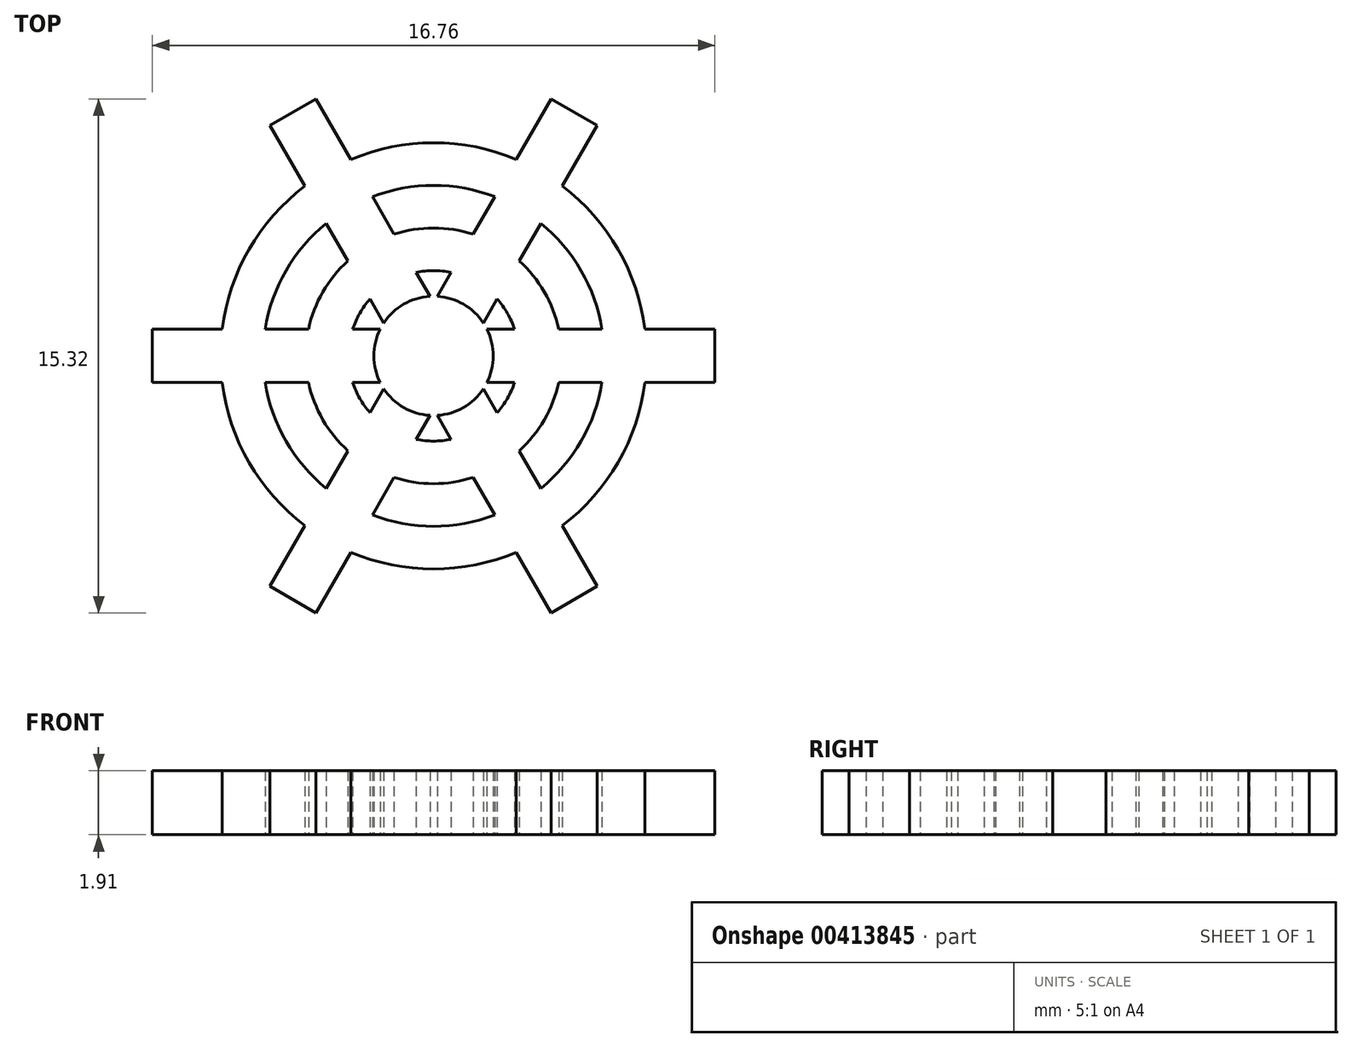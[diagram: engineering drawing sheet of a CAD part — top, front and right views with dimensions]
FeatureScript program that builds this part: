
annotation { "Feature Type Name" : "Feature", "Feature Type Description" : "" }
export const myFeature = defineFeature(function(context is Context, id is Id, definition is map)
    precondition{}
    {
        {
            var Q0;
            Q0=qCreatedBy(makeId("Top.planeOp"),FACE);
            var sketch = newSketch(context, id + "F0", { "sketchPlane" : qUnion([Q0])});
            skArc(sketch, "E0", {"start": v(-3.84, 5.06) * mm, "mid": v(-5.5, 3.17) * mm, "end": v(-6.3, 0.8) * mm});
            skArc(sketch, "E1", {"start": v(-3.2, 3.95) * mm, "mid": v(-4.4, 2.54) * mm, "end": v(-5.02, 0.8) * mm});
            skArc(sketch, "E2", {"start": v(-2.55, 2.83) * mm, "mid": v(-3.3, 1.9) * mm, "end": v(-3.73, 0.8) * mm});
            skArc(sketch, "E3", {"start": v(-1.9, 1.7) * mm, "mid": v(-2.2, 1.27) * mm, "end": v(-2.41, 0.8) * mm});
            skLineSegment(sketch, "E4.bottom", {"start": v(8.38, -0.8) * mm, "end": v(6.3, -0.8) * mm});
            skLineSegment(sketch, "E4.top", {"start": v(8.38, 0.8) * mm, "end": v(6.3, 0.8) * mm});
            skLineSegment(sketch, "E4.left", {"start": v(8.38, -0.8) * mm, "end": v(8.38, 0.8) * mm});
            skLineSegment(sketch, "E4.right", {"start": v(-8.38, -0.8) * mm, "end": v(-8.38, 0.8) * mm});
            skLineSegment(sketch, "E5.top", {"start": v(0.8, -8.38) * mm, "end": v(-0.8, -8.38) * mm});
            skLineSegment(sketch, "E6.1.1", {"start": v(-3.5, 7.66) * mm, "end": v(-2.46, 5.85) * mm});
            skLineSegment(sketch, "E6.1.2", {"start": v(-3.5, 7.66) * mm, "end": v(-4.88, 6.86) * mm});
            skLineSegment(sketch, "E6.1.3", {"start": v(-4.88, 6.86) * mm, "end": v(-3.84, 5.06) * mm});
            skLineSegment(sketch, "E6.1.4", {"start": v(4.88, -6.86) * mm, "end": v(3.5, -7.66) * mm});
            skLineSegment(sketch, "E6.2.1", {"start": v(-4.88, -6.86) * mm, "end": v(-3.84, -5.06) * mm});
            skLineSegment(sketch, "E6.2.2", {"start": v(-4.88, -6.86) * mm, "end": v(-3.5, -7.66) * mm});
            skLineSegment(sketch, "E6.2.3", {"start": v(-3.5, -7.66) * mm, "end": v(-2.46, -5.85) * mm});
            skLineSegment(sketch, "E6.2.4", {"start": v(3.5, 7.66) * mm, "end": v(4.88, 6.86) * mm});
            skLineSegment(sketch, "E7.trimOffspring", {"start": v(-3.2, 3.95) * mm, "end": v(-2.55, 2.83) * mm});
            skLineSegment(sketch, "E8.trimOffspring", {"start": v(-1.82, 4.74) * mm, "end": v(-1.18, 3.62) * mm});
            skLineSegment(sketch, "E9.trimOffspring", {"start": v(-1.9, 1.7) * mm, "end": v(-1.48, 0.98) * mm});
            skLineSegment(sketch, "E10.trimOffspring", {"start": v(-0.52, 2.49) * mm, "end": v(-0.1, 1.77) * mm});
            skArc(sketch, "E11.trimOffspring", {"start": v(-6.3, -0.8) * mm, "mid": v(-5.5, -3.17) * mm, "end": v(-3.84, -5.06) * mm});
            skArc(sketch, "E12.trimOffspring", {"start": v(-5.02, -0.8) * mm, "mid": v(-4.4, -2.54) * mm, "end": v(-3.2, -3.95) * mm});
            skLineSegment(sketch, "E13.trimOffspring", {"start": v(-6.3, 0.8) * mm, "end": v(-8.38, 0.8) * mm});
            skLineSegment(sketch, "E14.trimOffspring", {"start": v(-6.3, -0.8) * mm, "end": v(-8.38, -0.8) * mm});
            skArc(sketch, "E15.trimOffspring", {"start": v(-3.73, -0.8) * mm, "mid": v(-3.3, -1.9) * mm, "end": v(-2.55, -2.83) * mm});
            skLineSegment(sketch, "E16.trimOffspring", {"start": v(-3.73, 0.8) * mm, "end": v(-5.02, 0.8) * mm});
            skLineSegment(sketch, "E17.trimOffspring", {"start": v(-3.73, -0.8) * mm, "end": v(-5.02, -0.8) * mm});
            skArc(sketch, "E18.trimOffspring", {"start": v(-2.41, -0.8) * mm, "mid": v(-2.2, -1.27) * mm, "end": v(-1.9, -1.7) * mm});
            skLineSegment(sketch, "E19.trimOffspring", {"start": v(0.1, -1.77) * mm, "end": v(0.52, -2.49) * mm});
            skLineSegment(sketch, "E20.trimOffspring", {"start": v(-1.6, 0.8) * mm, "end": v(-2.41, 0.8) * mm});
            skLineSegment(sketch, "E21.trimOffspring", {"start": v(0.1, 1.77) * mm, "end": v(0.52, 2.49) * mm});
            skLineSegment(sketch, "E22.trimOffspring", {"start": v(-3.2, -3.95) * mm, "end": v(-2.55, -2.83) * mm});
            skArc(sketch, "E23.trimOffspring", {"start": v(-2.46, -5.85) * mm, "mid": v(0, -6.35) * mm, "end": v(2.46, -5.85) * mm});
            skLineSegment(sketch, "E24.trimOffspring", {"start": v(-1.82, -4.74) * mm, "end": v(-1.18, -3.62) * mm});
            skLineSegment(sketch, "E25.trimOffspring", {"start": v(2.46, -5.85) * mm, "end": v(3.5, -7.66) * mm});
            skArc(sketch, "E26.trimOffspring", {"start": v(3.84, -5.06) * mm, "mid": v(5.5, -3.17) * mm, "end": v(6.3, -0.8) * mm});
            skLineSegment(sketch, "E27.trimOffspring", {"start": v(3.84, -5.06) * mm, "end": v(4.88, -6.86) * mm});
            skLineSegment(sketch, "E28.trimOffspring", {"start": v(5.02, -0.8) * mm, "end": v(3.73, -0.8) * mm});
            skArc(sketch, "E29.trimOffspring", {"start": v(6.3, 0.8) * mm, "mid": v(5.5, 3.17) * mm, "end": v(3.84, 5.06) * mm});
            skLineSegment(sketch, "E30.trimOffspring", {"start": v(5.02, 0.8) * mm, "end": v(3.73, 0.8) * mm});
            skLineSegment(sketch, "E31.trimOffspring", {"start": v(3.84, 5.06) * mm, "end": v(4.88, 6.86) * mm});
            skArc(sketch, "E32.trimOffspring", {"start": v(2.46, 5.85) * mm, "mid": v(0, 6.35) * mm, "end": v(-2.46, 5.85) * mm});
            skLineSegment(sketch, "E33.trimOffspring", {"start": v(2.46, 5.85) * mm, "end": v(3.5, 7.66) * mm});
            skArc(sketch, "E34.trimOffspring", {"start": v(1.82, 4.74) * mm, "mid": v(0, 5.08) * mm, "end": v(-1.82, 4.74) * mm});
            skArc(sketch, "E35.trimOffspring", {"start": v(1.18, 3.62) * mm, "mid": v(0, 3.81) * mm, "end": v(-1.18, 3.62) * mm});
            skArc(sketch, "E36.trimOffspring", {"start": v(0.52, 2.49) * mm, "mid": v(0, 2.54) * mm, "end": v(-0.52, 2.49) * mm});
            skLineSegment(sketch, "E37.trimOffspring", {"start": v(1.18, 3.62) * mm, "end": v(1.82, 4.74) * mm});
            skLineSegment(sketch, "E38.trimOffspring", {"start": v(2.55, 2.83) * mm, "end": v(3.2, 3.95) * mm});
            skLineSegment(sketch, "E39.trimOffspring", {"start": v(2.41, 0.8) * mm, "end": v(1.6, 0.8) * mm});
            skLineSegment(sketch, "E40.trimOffspring", {"start": v(2.41, -0.8) * mm, "end": v(1.6, -0.8) * mm});
            skLineSegment(sketch, "E41.trimOffspring", {"start": v(2.55, -2.83) * mm, "end": v(3.2, -3.95) * mm});
            skLineSegment(sketch, "E42.trimOffspring", {"start": v(1.18, -3.62) * mm, "end": v(1.82, -4.74) * mm});
            skLineSegment(sketch, "E43.trimOffspring", {"start": v(-0.52, -2.49) * mm, "end": v(-0.1, -1.77) * mm});
            skLineSegment(sketch, "E44.trimOffspring", {"start": v(-1.9, -1.7) * mm, "end": v(-1.48, -0.98) * mm});
            skArc(sketch, "E45.trimOffspring", {"start": v(-1.18, -3.62) * mm, "mid": v(0, -3.81) * mm, "end": v(1.18, -3.62) * mm});
            skArc(sketch, "E46.trimOffspring", {"start": v(-1.82, -4.74) * mm, "mid": v(0, -5.08) * mm, "end": v(1.82, -4.74) * mm});
            skArc(sketch, "E47.trimOffspring", {"start": v(2.55, -2.83) * mm, "mid": v(3.3, -1.9) * mm, "end": v(3.73, -0.8) * mm});
            skArc(sketch, "E48.trimOffspring", {"start": v(3.2, -3.95) * mm, "mid": v(4.4, -2.54) * mm, "end": v(5.02, -0.8) * mm});
            skArc(sketch, "E49.trimOffspring", {"start": v(5.02, 0.8) * mm, "mid": v(4.4, 2.54) * mm, "end": v(3.2, 3.95) * mm});
            skArc(sketch, "E50.trimOffspring", {"start": v(3.73, 0.8) * mm, "mid": v(3.3, 1.9) * mm, "end": v(2.55, 2.83) * mm});
            skArc(sketch, "E51.trimOffspring", {"start": v(2.41, 0.8) * mm, "mid": v(2.2, 1.27) * mm, "end": v(1.9, 1.7) * mm});
            skLineSegment(sketch, "E52.trimOffspring", {"start": v(1.48, 0.98) * mm, "end": v(1.9, 1.7) * mm});
            skLineSegment(sketch, "E53.trimOffspring", {"start": v(1.48, -0.98) * mm, "end": v(1.9, -1.7) * mm});
            skLineSegment(sketch, "E54.trimOffspring", {"start": v(-1.6, -0.8) * mm, "end": v(-2.41, -0.8) * mm});
            skArc(sketch, "E55", {"start": v(-1.6, 0.8) * mm, "mid": v(-1.78, 0) * mm, "end": v(-1.6, -0.8) * mm});
            skArc(sketch, "E56.trimOffspring", {"start": v(-0.1, 1.77) * mm, "mid": v(-0.89, 1.54) * mm, "end": v(-1.48, 0.98) * mm});
            skArc(sketch, "E57.trimOffspring", {"start": v(1.48, 0.98) * mm, "mid": v(0.89, 1.54) * mm, "end": v(0.1, 1.77) * mm});
            skArc(sketch, "E58.trimOffspring", {"start": v(1.6, -0.8) * mm, "mid": v(1.78, 0) * mm, "end": v(1.6, 0.8) * mm});
            skArc(sketch, "E59.trimOffspring", {"start": v(0.1, -1.77) * mm, "mid": v(0.89, -1.54) * mm, "end": v(1.48, -0.98) * mm});
            skArc(sketch, "E60.trimOffspring", {"start": v(-1.48, -0.98) * mm, "mid": v(-0.89, -1.54) * mm, "end": v(-0.1, -1.77) * mm});
            skArc(sketch, "E61.trimOffspring", {"start": v(-0.52, -2.49) * mm, "mid": v(0, -2.54) * mm, "end": v(0.52, -2.49) * mm});
            skArc(sketch, "E62.trimOffspring", {"start": v(1.9, -1.7) * mm, "mid": v(2.2, -1.27) * mm, "end": v(2.41, -0.8) * mm});
            skSolve(sketch);
        }
        {
            var Q0;
            Q0=makeQuery(id+"F0.imprint","IMPRINT",FACE,{"disambiguationData":[TD([[makeQuery(id+"F0.imprint","IMPRINT",EDGE,{"derivedFrom":sQuery(id+"F0.wireOp",EDGE,"E0")}),1.0]])]});
            extrude(context, id + "F1", {"entities" : qUnion([Q0]), "depth" : 1.9 * mm});
        }
    });
